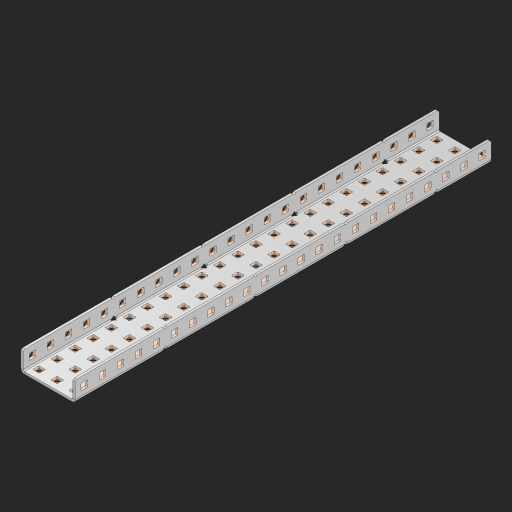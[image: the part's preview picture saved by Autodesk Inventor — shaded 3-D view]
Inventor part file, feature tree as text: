
AUTODESK INVENTOR PART (.ipt)
format: ipt  version: 2023 (Build 270158000, 158)  size: 1,490,944 bytes
history: native  units: in
note: dims shown in document units (in); Inventor stores cm internally (conversion verified against a paired STEP export)
features: other x120, extrude x114, sheet_metal_op x10, sketch x8, mirror x1, pattern_linear x1, chamfer x1
ambient origin geometry x8: Origin, YZ Plane, XZ Plane, XY Plane, X Axis, Y Axis, Z Axis, Center Point
bodies: Solid1 (feature_tree), Body (feature_tree)
feature tree (255):
  other  "Flange Pattern Plane"
  sheet_metal_op  "Flange Pattern"
  sheet_metal_op  "Body Pattern"
  other  "Arc Length"
  mirror  "Notch Mirror"
  pattern_linear  "Notch Pattern"  Spacing1=0.25in  [1 undecoded]
  chamfer  "End Chamfer"
  extrude  "Half Cut"  Depth=0.0625in
  sketch  "Sketch1"  dims[d0=1.5in]
  other  "Plate1"
  sketch  "Sketch2"  dims[d1=11.5in]
  other  "Plate2"
  sheet_metal_op  "Bend1"
  sheet_metal_op  "Corner1"
  sketch  "Sketch3"  dims[d2=0.0625in]
  other  "Flange Pattern Sketch"
  sketch  "Sketch7"  dims[d3=0.0625in]
  other  "Srf1"
  other  "Srf2"
  sketch  "Sketch8"  dims[d4=0.0312in]
  sketch  "Sketch9"  dims[d5=0.125in]
  other  "Srf91"
  sheet_metal_op  "Body Pattern Sketch"
  other  "Srf92"
  sketch  "Sketch13"  dims[d6=0.0625in]
  sketch  "Sketch14"  dims[d7=0.5in d8=90.0deg d9=0.0312in d10=0.25in d11=0.0625in d12=0.0625in d16=0.182in d17=0.02in d18=0.0625in d19=0.0in d20=0.25in d21=0.25in d46=0.172in d47=1.0in d48=0.0in d49=0.182in d50=0.02in d51=0.25in d52=0.25in d53=0.0625in d54=0.0in d55=0.172in d56=1.0in d57=0.0in d60=9.0551in d62=0.5in d63=1.1811in d65=0.5in d85=0.1473in d86=0.1782in d88=0.04in d89=0.0625in d90=0.0in d91=0.04in d92=0.0491in d95=2.5in d96=0.04in d97=0.25in d98=45.0deg d101=0.0in d102=2.497in d131=1.5in d132=9.0551in d134=0.5in d139=0.5in]
  other  "Srf856"
  other  "Srf1310"
  other  "Srf1311"
  other  "Srf1312"
  other  "Srf1376"
  other  "Srf1377"
  other  "Srf1728"
  other  "Srf1755"
  other  "Srf1878"
  other  "Srf1879"
  other  "Srf1880"
  other  "Srf1881"
  other  "Srf1882"
  other  "Srf1883"
  other  "Srf1884"
  other  "Srf1885"
  other  "Srf1886"
  other  "Srf1887"
  other  "Srf1888"
  other  "Srf1889"
  other  "Srf1890"
  other  "Srf1891"
  other  "Srf1892"
  other  "Srf1893"
  other  "Srf1894"
  other  "Srf1895"
  other  "Srf1896"
  other  "Srf1897"
  other  "Srf1898"
  other  "Srf1899"
  other  "Srf1900"
  other  "Srf1901"
  other  "Srf1902"
  other  "Srf1903"
  other  "Srf1904"
  other  "Srf1905"
  other  "Srf1906"
  other  "Srf1907"
  other  "Srf1908"
  other  "Srf1909"
  other  "Srf1910"
  other  "Srf1911"
  other  "Srf1912"
  other  "Srf1913"
  other  "Srf1914"
  other  "Srf1915"
  other  "Srf1916"
  other  "Srf1917"
  other  "Srf1942"
  other  "Srf1943"
  other  "Srf1944"
  other  "Srf1945"
  other  "Srf1946"
  other  "Srf1947"
  other  "Srf1948"
  other  "Srf1949"
  other  "Srf1950"
  other  "Srf1951"
  other  "Srf1952"
  other  "Srf1953"
  other  "Srf1954"
  other  "Srf1955"
  other  "Srf1956"
  other  "Srf1957"
  other  "Srf1958"
  other  "Srf1959"
  other  "Srf1960"
  other  "Srf1961"
  other  "Srf1962"
  other  "Srf1963"
  other  "Srf1964"
  other  "Srf1965"
  other  "Srf1966"
  other  "Srf1967"
  other  "Srf1968"
  other  "Srf1969"
  other  "Srf1970"
  other  "Srf1971"
  other  "Srf1972"
  other  "Srf1973"
  other  "Srf1974"
  other  "Srf1975"
  other  "Srf1976"
  other  "Srf1977"
  other  "Srf1978"
  other  "Srf1979"
  other  "Srf1980"
  other  "Srf1981"
  other  "Srf1982"
  other  "Srf1983"
  other  "Srf1984"
  other  "Srf1985"
  other  "Srf1986"
  other  "Srf1987"
  other  "Srf1988"
  other  "Srf1989"
  other  "Srf1990"
  other  "Srf1991"
  other  "Srf1992"
  other  "Srf1993"
  other  "Srf1994"
  other  "Srf1995"
  other  "Srf1996"
  other  "Srf1997"
  other  "Srf1998"
  other  "Srf1999"
  other  "Srf2000"
  other  "Srf2001"
  other  "Srf2002"
  other  "Srf2003"
  other  "Srf2004"
  sheet_metal_op  "Flange Stamp"
  sheet_metal_op  "Flange Circle"
  sheet_metal_op  "Body Stamp"
  sheet_metal_op  "Body Circle"
  sheet_metal_op  "Notch"
  extrude  "ExtrusionSrf2"  Depth=0.0625in
  extrude  "ExtrusionSrf92"  Depth=1.5in
  extrude  "ExtrusionSrf856"  Depth=0.02in
  extrude  "ExtrusionSrf1310"  Depth=0.0625in
  extrude  "ExtrusionSrf1311"  TaperAngle=0.0deg  [1 undecoded]
  extrude  "ExtrusionSrf1312"  Depth=0.25in
  extrude  "ExtrusionSrf1376"  Depth=0.25in
  extrude  "ExtrusionSrf1377"  Depth=1.5in
  extrude  "ExtrusionSrf1728"  Depth=1.5in TaperAngle=0.0deg
  extrude  "ExtrusionSrf1755"  Depth=1.5in
  extrude  "ExtrusionSrf1878"  Depth=0.02in
  extrude  "ExtrusionSrf1879"  Depth=0.25in
  extrude  "ExtrusionSrf1880"  Depth=0.25in
  extrude  "ExtrusionSrf1881"  Depth=0.0625in
  extrude  "ExtrusionSrf1882"  TaperAngle=0.0deg  [1 undecoded]
  extrude  "ExtrusionSrf1883"  Depth=1.5in
  extrude  "ExtrusionSrf1884"  Depth=1.5in TaperAngle=0.0deg
  extrude  "ExtrusionSrf1885"  Depth=1.5in
  extrude  "ExtrusionSrf1886"  Depth=1.5in
  extrude  "ExtrusionSrf1887"  Depth=1.5in
  extrude  "ExtrusionSrf1888"  Depth=1.5in
  extrude  "ExtrusionSrf1889"  Depth=1.5in
  extrude  "ExtrusionSrf1890"  Depth=0.0625in
  extrude  "ExtrusionSrf1891"  TaperAngle=0.0deg  [1 undecoded]
  extrude  "ExtrusionSrf1892"  Depth=1.5in
  extrude  "ExtrusionSrf1893"  Depth=1.5in
  extrude  "ExtrusionSrf1894"  Depth=1.5in
  extrude  "ExtrusionSrf1895"  Depth=0.25in TaperAngle=45.0deg
  extrude  "ExtrusionSrf1896"  TaperAngle=0.0deg  [1 undecoded]
  extrude  "ExtrusionSrf1897"  Depth=1.5in
  extrude  "ExtrusionSrf1898"  Depth=1.5in
  extrude  "ExtrusionSrf1899"  Depth=1.5in
  extrude  "ExtrusionSrf1900"  Depth=1.5in
  extrude  "ExtrusionSrf1901"  Depth=1.5in
  extrude  "ExtrusionSrf1902"  [1 undecoded]
  extrude  "ExtrusionSrf1903"  [1 undecoded]
  extrude  "ExtrusionSrf1904"  [1 undecoded]
  extrude  "ExtrusionSrf1905"  [1 undecoded]
  extrude  "ExtrusionSrf1906"  [1 undecoded]
  extrude  "ExtrusionSrf1907"  [1 undecoded]
  extrude  "ExtrusionSrf1908"  [1 undecoded]
  extrude  "ExtrusionSrf1909"  [1 undecoded]
  extrude  "ExtrusionSrf1910"  [1 undecoded]
  extrude  "ExtrusionSrf1911"  [1 undecoded]
  extrude  "ExtrusionSrf1912"  [1 undecoded]
  extrude  "ExtrusionSrf1913"  [1 undecoded]
  extrude  "ExtrusionSrf1914"  [1 undecoded]
  extrude  "ExtrusionSrf1915"  [1 undecoded]
  extrude  "ExtrusionSrf1916"  [1 undecoded]
  extrude  "ExtrusionSrf1917"  [1 undecoded]
  extrude  "ExtrusionSrf1942"  [1 undecoded]
  extrude  "ExtrusionSrf1943"  [1 undecoded]
  extrude  "ExtrusionSrf1944"  [1 undecoded]
  extrude  "ExtrusionSrf1945"  [1 undecoded]
  extrude  "ExtrusionSrf1946"  [1 undecoded]
  extrude  "ExtrusionSrf1947"  [1 undecoded]
  extrude  "ExtrusionSrf1948"  [1 undecoded]
  extrude  "ExtrusionSrf1949"  [1 undecoded]
  extrude  "ExtrusionSrf1950"  [1 undecoded]
  extrude  "ExtrusionSrf1951"  [1 undecoded]
  extrude  "ExtrusionSrf1952"  [1 undecoded]
  extrude  "ExtrusionSrf1953"  [1 undecoded]
  extrude  "ExtrusionSrf1954"  [1 undecoded]
  extrude  "ExtrusionSrf1955"  [1 undecoded]
  extrude  "ExtrusionSrf1956"  [1 undecoded]
  extrude  "ExtrusionSrf1957"  [1 undecoded]
  extrude  "ExtrusionSrf1958"  [1 undecoded]
  extrude  "ExtrusionSrf1959"  [1 undecoded]
  extrude  "ExtrusionSrf1960"  [1 undecoded]
  extrude  "ExtrusionSrf1961"  [1 undecoded]
  extrude  "ExtrusionSrf1962"  [1 undecoded]
  extrude  "ExtrusionSrf1963"  [1 undecoded]
  extrude  "ExtrusionSrf1964"  [1 undecoded]
  extrude  "ExtrusionSrf1965"  [1 undecoded]
  extrude  "ExtrusionSrf1966"  [1 undecoded]
  extrude  "ExtrusionSrf1967"  [1 undecoded]
  extrude  "ExtrusionSrf1968"  [1 undecoded]
  extrude  "ExtrusionSrf1969"  [1 undecoded]
  extrude  "ExtrusionSrf1970"  [1 undecoded]
  extrude  "ExtrusionSrf1971"  [1 undecoded]
  extrude  "ExtrusionSrf1972"  [1 undecoded]
  extrude  "ExtrusionSrf1973"  [1 undecoded]
  extrude  "ExtrusionSrf1974"  [1 undecoded]
  extrude  "ExtrusionSrf1975"  [1 undecoded]
  extrude  "ExtrusionSrf1976"  [1 undecoded]
  extrude  "ExtrusionSrf1977"  [1 undecoded]
  extrude  "ExtrusionSrf1978"  [1 undecoded]
  extrude  "ExtrusionSrf1979"  [1 undecoded]
  extrude  "ExtrusionSrf1980"  [1 undecoded]
  extrude  "ExtrusionSrf1981"  [1 undecoded]
  extrude  "ExtrusionSrf1982"  [1 undecoded]
  extrude  "ExtrusionSrf1983"  [1 undecoded]
  extrude  "ExtrusionSrf1984"  [1 undecoded]
  extrude  "ExtrusionSrf1985"  [1 undecoded]
  extrude  "ExtrusionSrf1986"  [1 undecoded]
  extrude  "ExtrusionSrf1987"  [1 undecoded]
  extrude  "ExtrusionSrf1988"  [1 undecoded]
  extrude  "ExtrusionSrf1989"  [1 undecoded]
  extrude  "ExtrusionSrf1990"  [1 undecoded]
  extrude  "ExtrusionSrf1991"  [1 undecoded]
  extrude  "ExtrusionSrf1992"  [1 undecoded]
  extrude  "ExtrusionSrf1993"  [1 undecoded]
  extrude  "ExtrusionSrf1994"  [1 undecoded]
  extrude  "ExtrusionSrf1995"  [1 undecoded]
  extrude  "ExtrusionSrf1996"  [1 undecoded]
  extrude  "ExtrusionSrf1997"  [1 undecoded]
  extrude  "ExtrusionSrf1998"  [1 undecoded]
  extrude  "ExtrusionSrf1999"  [1 undecoded]
  extrude  "ExtrusionSrf2000"  [1 undecoded]
  extrude  "ExtrusionSrf2001"  [1 undecoded]
  extrude  "ExtrusionSrf2002"  [1 undecoded]
  extrude  "ExtrusionSrf2003"  [1 undecoded]
  extrude  "ExtrusionSrf2004"  [1 undecoded]
note: 84 required parameter values undecoded (feature->parameter linkage not recoverable at this tier; creation-order binding heuristic only, values carry confidence <= 0.55)
